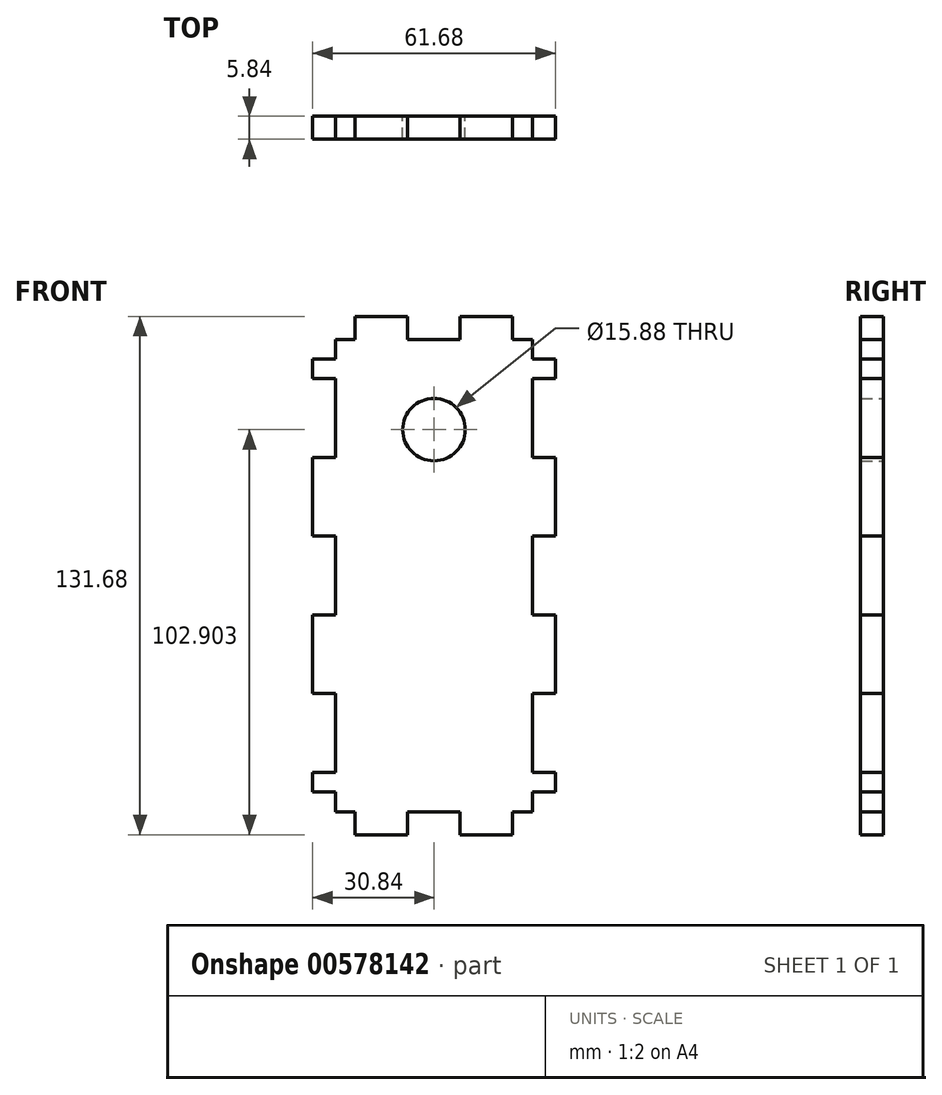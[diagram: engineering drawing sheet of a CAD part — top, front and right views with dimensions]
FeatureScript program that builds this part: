
annotation { "Feature Type Name" : "Feature", "Feature Type Description" : "" }
export const myFeature = defineFeature(function(context is Context, id is Id, definition is map)
    precondition{}
    {
        {
            var Q0;
            Q0=qCreatedBy(makeId("Front.planeOp"),FACE);
            var sketch = newSketch(context, id + "F0", { "sketchPlane" : qUnion([Q0])});
            skLineSegment(sketch, "E0.bottom", {"start": v(-25, 60) * mm, "end": v(25, 60) * mm});
            skLineSegment(sketch, "E0.top", {"start": v(-25, -60) * mm, "end": v(25, -60) * mm});
            skLineSegment(sketch, "E0.left", {"start": v(-25, 60) * mm, "end": v(-25, -60) * mm});
            skLineSegment(sketch, "E0.right", {"start": v(25, 60) * mm, "end": v(25, -60) * mm});
            skLineSegment(sketch, "E1.left", {"start": v(30.84, 55) * mm, "end": v(30.84, 50) * mm});
            skLineSegment(sketch, "E1.right", {"start": v(-30.84, 55) * mm, "end": v(-30.84, 50) * mm});
            skPoint(sketch, "E1.middle", {"position": v(0, 0) * mm});
            skLineSegment(sketch, "E2.left", {"start": v(6.67, -65.84) * mm, "end": v(6.67, -60) * mm});
            skLineSegment(sketch, "E2.right", {"start": v(-6.67, -65.84) * mm, "end": v(-6.67, -60) * mm});
            skPoint(sketch, "E2.middle", {"position": v(0, -60) * mm});
            skPoint(sketch, "E3.middle", {"position": v(-25, -60) * mm});
            skLineSegment(sketch, "E4.left", {"start": v(-6.67, 65.84) * mm, "end": v(-6.67, 60) * mm});
            skLineSegment(sketch, "E4.right", {"start": v(6.67, 65.84) * mm, "end": v(6.67, 60) * mm});
            skPoint(sketch, "E4.middle", {"position": v(0, 60) * mm});
            skPoint(sketch, "E5.middle", {"position": v(-25, 60) * mm});
            skPoint(sketch, "E6.middle", {"position": v(25, 60) * mm});
            skLineSegment(sketch, "E7.bottom", {"start": v(-6.67, 60) * mm, "end": v(-20, 60) * mm});
            skLineSegment(sketch, "E7.left", {"start": v(-6.67, 60) * mm, "end": v(-6.67, 65.84) * mm});
            skLineSegment(sketch, "E7.right", {"start": v(-20, 60) * mm, "end": v(-20, 65.84) * mm});
            skLineSegment(sketch, "E8.bottom", {"start": v(6.67, 60) * mm, "end": v(20, 60) * mm});
            skLineSegment(sketch, "E8.left", {"start": v(6.67, 60) * mm, "end": v(6.67, 65.84) * mm});
            skLineSegment(sketch, "E8.right", {"start": v(20, 60) * mm, "end": v(20, 65.84) * mm});
            skLineSegment(sketch, "E9.bottom", {"start": v(-6.67, -60) * mm, "end": v(-20, -60) * mm});
            skLineSegment(sketch, "E9.left", {"start": v(-6.67, -60) * mm, "end": v(-6.67, -65.84) * mm});
            skLineSegment(sketch, "E9.right", {"start": v(-20, -60) * mm, "end": v(-20, -65.84) * mm});
            skLineSegment(sketch, "E10.bottom", {"start": v(6.67, -60) * mm, "end": v(20, -60) * mm});
            skLineSegment(sketch, "E10.left", {"start": v(6.67, -60) * mm, "end": v(6.67, -65.84) * mm});
            skLineSegment(sketch, "E10.right", {"start": v(20, -60) * mm, "end": v(20, -65.84) * mm});
            skPoint(sketch, "E11.orphan", {"position": v(-6.67, 54.16) * mm});
            skPoint(sketch, "E12.orphan", {"position": v(6.67, 54.16) * mm});
            skPoint(sketch, "E13.orphan", {"position": v(-6.67, -54.16) * mm});
            skPoint(sketch, "E14.orphan", {"position": v(6.67, -54.16) * mm});
            skLineSegment(sketch, "E15.bottom", {"start": v(-25, 10) * mm, "end": v(-30.84, 10) * mm});
            skLineSegment(sketch, "E15.top", {"start": v(-25, -10) * mm, "end": v(-30.84, -10) * mm});
            skLineSegment(sketch, "E15.left", {"start": v(-25, 10) * mm, "end": v(-25, -10) * mm});
            skPoint(sketch, "E15.middle", {"position": v(-30.84, 0) * mm});
            skLineSegment(sketch, "E16.bottom", {"start": v(-30.84, 10) * mm, "end": v(-25, 10) * mm});
            skLineSegment(sketch, "E16.top", {"start": v(-30.84, 30) * mm, "end": v(-25, 30) * mm});
            skLineSegment(sketch, "E16.right", {"start": v(-25, 10) * mm, "end": v(-25, 30) * mm});
            skPoint(sketch, "E16.middle", {"position": v(-30.84, 20) * mm});
            skLineSegment(sketch, "E17.bottom", {"start": v(-30.84, -10) * mm, "end": v(-25, -10) * mm});
            skLineSegment(sketch, "E17.top", {"start": v(-30.84, -30) * mm, "end": v(-25, -30) * mm});
            skLineSegment(sketch, "E17.right", {"start": v(-25, -10) * mm, "end": v(-25, -30) * mm});
            skPoint(sketch, "E17.middle", {"position": v(-30.84, -20) * mm});
            skLineSegment(sketch, "E18.top", {"start": v(-30.84, 50) * mm, "end": v(-25, 50) * mm});
            skLineSegment(sketch, "E18.right", {"start": v(-25, 30) * mm, "end": v(-25, 50) * mm});
            skPoint(sketch, "E18.middle", {"position": v(-30.84, 40) * mm});
            skPoint(sketch, "E19.cornerSnap0", {"position": v(-36.68, 20) * mm});
            skLineSegment(sketch, "E20.top", {"start": v(-30.84, -50) * mm, "end": v(-25, -50) * mm});
            skLineSegment(sketch, "E20.right", {"start": v(-25, -30) * mm, "end": v(-25, -50) * mm});
            skPoint(sketch, "E20.middle", {"position": v(-30.84, -40) * mm});
            skLineSegment(sketch, "E21.bottom", {"start": v(-25, 55) * mm, "end": v(-30.84, 55) * mm});
            skLineSegment(sketch, "E21.top", {"start": v(-25, 50) * mm, "end": v(-30.84, 50) * mm});
            skLineSegment(sketch, "E21.left", {"start": v(-25, 55) * mm, "end": v(-25, 50) * mm});
            skLineSegment(sketch, "E22.bottom", {"start": v(-25, -50) * mm, "end": v(-30.84, -50) * mm});
            skLineSegment(sketch, "E22.top", {"start": v(-25, -55) * mm, "end": v(-30.84, -55) * mm});
            skLineSegment(sketch, "E22.left", {"start": v(-25, -50) * mm, "end": v(-25, -55) * mm});
            skLineSegment(sketch, "E23.bottom", {"start": v(25, 10) * mm, "end": v(30.84, 10) * mm});
            skLineSegment(sketch, "E23.top", {"start": v(25, -10) * mm, "end": v(30.84, -10) * mm});
            skLineSegment(sketch, "E23.left", {"start": v(25, 10) * mm, "end": v(25, -10) * mm});
            skPoint(sketch, "E23.middle", {"position": v(30.84, 0) * mm});
            skLineSegment(sketch, "E24.bottom", {"start": v(30.84, 10) * mm, "end": v(25, 10) * mm});
            skLineSegment(sketch, "E24.top", {"start": v(30.84, 30) * mm, "end": v(25, 30) * mm});
            skLineSegment(sketch, "E24.right", {"start": v(25, 10) * mm, "end": v(25, 30) * mm});
            skPoint(sketch, "E24.middle", {"position": v(30.84, 20) * mm});
            skLineSegment(sketch, "E25.bottom", {"start": v(30.84, -10) * mm, "end": v(25, -10) * mm});
            skLineSegment(sketch, "E25.top", {"start": v(30.84, -30) * mm, "end": v(25, -30) * mm});
            skLineSegment(sketch, "E25.right", {"start": v(25, -10) * mm, "end": v(25, -30) * mm});
            skPoint(sketch, "E25.middle", {"position": v(30.84, -20) * mm});
            skLineSegment(sketch, "E26.top", {"start": v(30.84, 50) * mm, "end": v(25, 50) * mm});
            skLineSegment(sketch, "E26.right", {"start": v(25, 30) * mm, "end": v(25, 50) * mm});
            skPoint(sketch, "E26.middle", {"position": v(30.84, 40) * mm});
            skLineSegment(sketch, "E27.top", {"start": v(30.84, -50) * mm, "end": v(25, -50) * mm});
            skLineSegment(sketch, "E27.right", {"start": v(25, -30) * mm, "end": v(25, -50) * mm});
            skPoint(sketch, "E27.middle", {"position": v(30.84, -40) * mm});
            skLineSegment(sketch, "E28.bottom", {"start": v(25, -50) * mm, "end": v(30.84, -50) * mm});
            skLineSegment(sketch, "E28.top", {"start": v(25, -55) * mm, "end": v(30.84, -55) * mm});
            skLineSegment(sketch, "E28.left", {"start": v(25, -50) * mm, "end": v(25, -55) * mm});
            skLineSegment(sketch, "E29.bottom", {"start": v(25, 55) * mm, "end": v(30.84, 55) * mm});
            skLineSegment(sketch, "E29.top", {"start": v(25, 50) * mm, "end": v(30.84, 50) * mm});
            skLineSegment(sketch, "E29.left", {"start": v(25, 55) * mm, "end": v(25, 50) * mm});
            skPoint(sketch, "E30.orphan", {"position": v(-36.68, 50) * mm});
            skPoint(sketch, "E31.orphan", {"position": v(-36.68, 30) * mm});
            skPoint(sketch, "E32.orphan", {"position": v(-36.68, 10) * mm});
            skPoint(sketch, "E33.orphan", {"position": v(-36.68, -10) * mm});
            skPoint(sketch, "E34.orphan", {"position": v(-36.68, -30) * mm});
            skPoint(sketch, "E22.right.end.orphan", {"position": v(-36.68, -55) * mm});
            skPoint(sketch, "E35.orphan", {"position": v(-36.68, -50) * mm});
            skPoint(sketch, "E36.orphan", {"position": v(36.68, 10) * mm});
            skPoint(sketch, "E37.orphan", {"position": v(36.68, -10) * mm});
            skPoint(sketch, "E38.orphan", {"position": v(36.68, -30) * mm});
            skPoint(sketch, "E39.orphan", {"position": v(36.68, -50) * mm});
            skPoint(sketch, "E40.orphan", {"position": v(36.68, -55) * mm});
            skPoint(sketch, "E41.orphan", {"position": v(36.68, 50) * mm});
            skPoint(sketch, "E42.orphan", {"position": v(36.68, 30) * mm});
            skLineSegment(sketch, "E43.bottom", {"start": v(-20, 60) * mm, "end": v(-6.67, 60) * mm});
            skLineSegment(sketch, "E43.top", {"start": v(-20, 65.84) * mm, "end": v(-6.67, 65.84) * mm});
            skLineSegment(sketch, "E44.top", {"start": v(6.67, 65.84) * mm, "end": v(20, 65.84) * mm});
            skLineSegment(sketch, "E45.top", {"start": v(-6.67, -65.84) * mm, "end": v(-20, -65.84) * mm});
            skLineSegment(sketch, "E46.top", {"start": v(6.67, -65.84) * mm, "end": v(20, -65.84) * mm});
            skPoint(sketch, "E47.orphan", {"position": v(30.84, 65.84) * mm});
            skPoint(sketch, "E48.orphan", {"position": v(-30.84, 65.84) * mm});
            skLineSegment(sketch, "E49.trimOffspring", {"start": v(-30.84, 30) * mm, "end": v(-30.84, 10) * mm});
            skLineSegment(sketch, "E50.trimOffspring", {"start": v(-30.84, -10) * mm, "end": v(-30.84, -30) * mm});
            skLineSegment(sketch, "E51.trimOffspring", {"start": v(-30.84, -40) * mm, "end": v(-30.84, -55) * mm});
            skPoint(sketch, "E52.trimOffspring.end.orphan", {"position": v(-30.84, -65.84) * mm});
            skPoint(sketch, "E53.orphan", {"position": v(30.84, -65.84) * mm});
            skLineSegment(sketch, "E54.trimOffspring", {"start": v(30.84, -50) * mm, "end": v(30.84, -55) * mm});
            skLineSegment(sketch, "E55.trimOffspring", {"start": v(30.84, -10) * mm, "end": v(30.84, -30) * mm});
            skLineSegment(sketch, "E56.trimOffspring", {"start": v(30.84, 30) * mm, "end": v(30.84, 10) * mm});
            skCircle(sketch, "E57", {"center": v(0, 37.06) * mm, "radius": 7.94 * mm});
            skSolve(sketch);
        }
        {
            var Q0;
            Q0=qSketchRegion(id+"F0",true);
            extrude(context, id + "F1", {"entities" : qUnion([Q0]), "depth" : 5.84 * mm, "offsetDistance" : 25 * mm});
        }
    });
